# Revit family: Deckel für Bogen variabel Magic
name_source: partatom
category: Generic Models
revit_build: Autodesk Revit 2015 (Build: 20140606_1530(x64)
units: mm (PartAtom-declared; Revit-internal decimal feet)

## types (13) — shared parameters
Length = 1 mm  [stored 0.00328084 ft]
Length 1 = 2 mm  [stored 0.00656168 ft]
Manufacturer = OBO Bettermann
URL = http://www.obo-bettermann.com
Width = 48 mm  [stored 0.15748 ft]
Width 1 = 24 mm  [stored 0.0787402 ft]
Width 2 = 88 mm  [stored 0.288714 ft]
Width/2 = 44 mm  [stored 0.144357 ft]

## per-type parameters (varying)
| type | GTIN | Height | Height 1 | Manufacturer Art.No. | Material | Radius |
| DFBMV 100 FS | 4012196040544 | 100 mm  [stored 0.328084 ft] | 60 mm  [stored 0.19685 ft] | 6040760 | Strip-galvanised | 100 mm  [stored 0.328084 ft] |
| DFBMV 150 FS | 4012196040551 | 150 mm | 96 mm | 6040762 | Strip-galvanised | 150 mm |
| DFBMV 200 FS | 4012196040599 | 200 mm  [stored 0.656168 ft] | 131 mm | 6040764 | Strip-galvanised | 200 mm  [stored 0.656168 ft] |
| DFBMV 300 FS | 4012196040605 | 300 mm | 202 mm | 6040766 | Strip-galvanised | 300 mm |
| DFBMV 400 FS | 4012196040629 | 400 mm  [stored 1.31234 ft] | 273 mm | 6040768 | Strip-galvanised | 400 mm  [stored 1.31234 ft] |
| DFBMV 500 FS | 4012196040674 | 500 mm  [stored 1.64042 ft] | 343 mm | 6040770 | Strip-galvanised | 500 mm  [stored 1.64042 ft] |
| DFBMV 600 FS | 4012196040711 | 600 mm | 414 mm | 6040772 | Strip-galvanised | 600 mm |
| DFBMV 100 DD | 4012196040728 | 100 mm  [stored 0.328084 ft] | 60 mm  [stored 0.19685 ft] | 6040780 | Strip galvanised zinc/aluminium, Double Dip | 100 mm  [stored 0.328084 ft] |
| DFBMV 200 DD | 4012196040797 | 200 mm  [stored 0.656168 ft] | 131 mm | 6040784 | Strip galvanised zinc/aluminium, Double Dip | 200 mm  [stored 0.656168 ft] |
| DFBMV 300 DD | 4012196040834 | 300 mm | 202 mm | 6040786 | Strip galvanised zinc/aluminium, Double Dip | 300 mm |
| DFBMV 400 DD | 4012196040841 | 400 mm  [stored 1.31234 ft] | 273 mm | 6040788 | Strip galvanised zinc/aluminium, Double Dip | 400 mm  [stored 1.31234 ft] |
| DFBMV 500 DD | 4012196040865 | 500 mm  [stored 1.64042 ft] | 343 mm | 6040790 | Strip galvanised zinc/aluminium, Double Dip | 500 mm  [stored 1.64042 ft] |
| DFBMV 600 DD | 4012196040896 | 600 mm | 414 mm | 6040792 | Strip galvanised zinc/aluminium, Double Dip | 600 mm |

note: column(s) folded — value = type name in every type: Article Type

note: [stored X ft] marks values corroborated as IEEE doubles in the binary element streams (Revit-internal decimal feet)

## geometry (parser evidence)
native form markers: Sweep x2
no freeform markers — native parametric forms only
